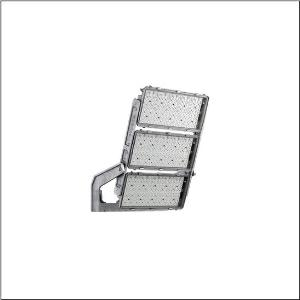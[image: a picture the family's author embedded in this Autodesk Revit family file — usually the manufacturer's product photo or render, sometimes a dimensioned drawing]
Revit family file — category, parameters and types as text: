
# Revit family: floodlight_fl_11_maxi_pro_remote___pl64_5xa779425v01aa_e912
name_source: partatom
category: Lighting Fixtures
units: mm (PartAtom-declared; Revit-internal decimal feet)

## family parameters
Cut with Voids When Loaded = No
Host = Face
Light Source = No
Part Type = Normal
Room Calculation Point = No
Round Connector Dimension = Use Diameter
Shared = No

## types (1)
- --- (1 x LED, 206660 lm, 1539.3 W, 3000K)
    Apparent Load = 1539 VA
    CIE Flux Codes = 28 79 98 100 100
    Color Rendering = 70
    Color Temperature = 3000K
    Default Elevation = 1800 mm
    Description = Floodlight FL 11  maxi  pro Remote floodlight; light control with lens of PMMA; cover panel of toughened safety glass, transparent; light distribution: PL64, asymmetric direct distribution, LEDcolour temperature: 3000K, rated luminous flux: 206.660lm, colour rendering: CRI > 70, light colour: 730; luminous efficacy: 134lm/W; brightness control: DALI 2 (1 DALI address); with terminal, 8-pole, max. 2.5mm², mains connection: 220..240V/380..400V AC, 50/60Hz, surge voltage resistance: line to ground: 10kV, ECG replaceable separately, no afterglow with DALI off / DMX off command, LED unit replaceable without ESD environment, dustproof LED module, dimming range 10..100%; 1539W floodlight with 2x LED unit of diecast aluminium, coated grey; length: 713mm / width: 651mm / height: 338mm; mounting bracket, of diecast aluminium, uncoated, natural, equipment: Power, protection rating (complete): IP66; insulation class (complete): insulation class I (protective earthing); certification: CE, ENEC, VDE; ball protection: ball impact resistance with accessories, impact resistance: IK07; only for outdoor installations, rated ambient temperature 10°C, permissible operating ambient temperature: -40..+30°C, permissible storage temperature: -40..+85°C; packaging unit: 1 piece

Light Distribution: PL64
    Height = 320 mm
    Lamp = 1 x LED
    Lamp Light Flux = 206660 lm
    Lamp Power = 1539.3 W
    Lamp count = 1
    Length = 1002 mm
    Luminous efficacy = 134 lm/W
    Manufacturer = Siteco
    ModVariant = No
    Model = 5XA779425V01AA
    Mounting Place = Ceiling
    Mounting Type = Surface mounted
    Number of Poles = 1
    OnlyDefault = Yes
    Power Factor = 1
    Product Name = Floodlight FL 11 maxi pro Remote | PL64
    Product group = floodlight | ceiling mounted
    ProductGroupID = 302
    Protection Class = Protection class I
    Protection Degree = IP 66
    RLX_Detail_Level = 1
    RLX_Emergency_Light_Flux = 0 lm
    RLX_Emergency_Type = 0
    RLX_Emergency_Type_DB = No
    RlxData = <blob elided: 52565 chars, md5=b099e4a5>
    Socket = socket
    Standby Power = 0 W
    System Light Flux = 206660 lm
    System Power = 1539 W
    Type Comments = factory setting: luminous flux: 100 % | dim-lin: 254 | 1080 mA
    Type Image = l_1006784.jpg
    URL = http://relux.com
    VarID = @adj_033069
    Voltage = 0 V
    Weight = 0.00 kg
    Width = 655 mm

## geometry (parser evidence)
native form markers: Blend x4, Sweep x11
no freeform markers — native parametric forms only
